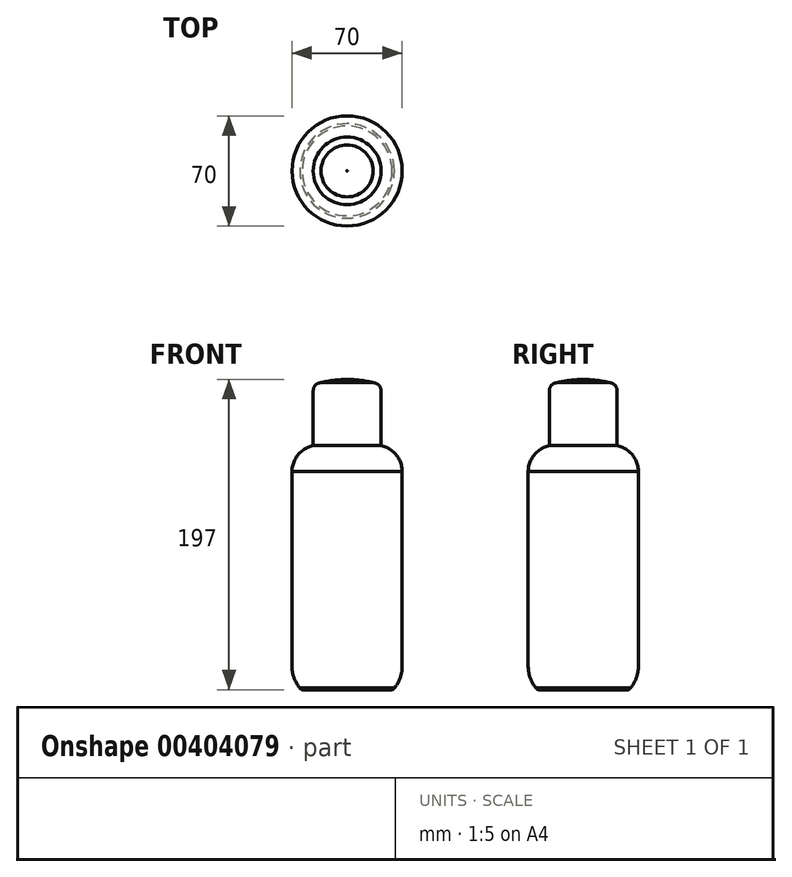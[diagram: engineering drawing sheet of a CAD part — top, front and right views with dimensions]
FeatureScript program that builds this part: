
annotation { "Feature Type Name" : "Feature", "Feature Type Description" : "" }
export const myFeature = defineFeature(function(context is Context, id is Id, definition is map)
    precondition{}
    {
        {
            var Q0;
            Q0=qCreatedBy(makeId("Front.planeOp"),FACE);
            var sketch = newSketch(context, id + "F0", { "sketchPlane" : qUnion([Q0])});
            skLineSegment(sketch, "E0.bottom", {"start": v(0, 0) * mm, "end": v(28.52, 0) * mm});
            skLineSegment(sketch, "E0.top", {"start": v(0, 155) * mm, "end": v(21.5, 155) * mm});
            skLineSegment(sketch, "E0.left", {"start": v(0, 0) * mm, "end": v(0, 155) * mm});
            skLineSegment(sketch, "E1.left", {"start": v(0, 155) * mm, "end": v(0, 195) * mm});
            skLineSegment(sketch, "E1.right", {"start": v(21.5, 155) * mm, "end": v(21.5, 190) * mm});
            skPoint(sketch, "E2.visualSharp", {"position": v(21.5, 195) * mm});
            skArc(sketch, "E2.filletArc", {"start": v(21.5, 190) * mm, "mid": v(20.04, 193.54) * mm, "end": v(16.5, 195) * mm});
            skLineSegment(sketch, "E3", {"start": v(0, 195) * mm, "end": v(0, 197) * mm});
            skArc(sketch, "E4", {"start": v(16.5, 195) * mm, "mid": v(8.3, 196.5) * mm, "end": v(0, 197) * mm});
            skArc(sketch, "E5", {"start": v(35, 138) * mm, "mid": v(31.32, 148.94) * mm, "end": v(21.5, 155) * mm});
            skArc(sketch, "E6", {"start": v(28, 0) * mm, "mid": v(29.15, 0.2) * mm, "end": v(30, 1) * mm});
            skArc(sketch, "E7", {"start": v(30, 1) * mm, "mid": v(33.71, 7.55) * mm, "end": v(35, 14.96) * mm});
            skLineSegment(sketch, "E8.trimOffspring", {"start": v(35, 14.96) * mm, "end": v(35, 138.73) * mm});
            skPoint(sketch, "E9.orphan", {"position": v(30, 0) * mm});
            skPoint(sketch, "E10.start.orphan", {"position": v(30, 2) * mm});
            skSolve(sketch);
        }
        {
            var Q0;
            Q0=makeQuery(id+"F0.imprint","IMPRINT",FACE,{"disambiguationData":[TD([[makeQuery(id+"F0.imprint","IMPRINT",EDGE,{"derivedFrom":sQuery(id+"F0.wireOp",EDGE,"E0.top")}),1.0]])]});
            var Q1;
            Q1=sQuery(id+"F0.wireOp",EDGE,"E1.left");
            revolve(context, id + "F1", {"entities" : qUnion([Q0]), "axis" : qUnion([Q1]), "revolveType" : RevolveType.FULL});
        }
        {
            var Q0;
            {var subQ5=sQuery(id+"F0.wireOp",EDGE,"E0.left");Q0=makeQuery(id+"F0.imprint","IMPRINT",FACE,{"disambiguationData":[TD([[makeQuery(id+"F0.imprint","IMPRINT",EDGE,{"derivedFrom":subQ5}),-1.0]])]});}
            var Q1;
            Q1=sQuery(id+"F0.wireOp",EDGE,"E0.left");
            revolve(context, id + "F2", {"entities" : qUnion([Q0]), "axis" : qUnion([Q1]), "revolveType" : RevolveType.FULL});
        }
    });
